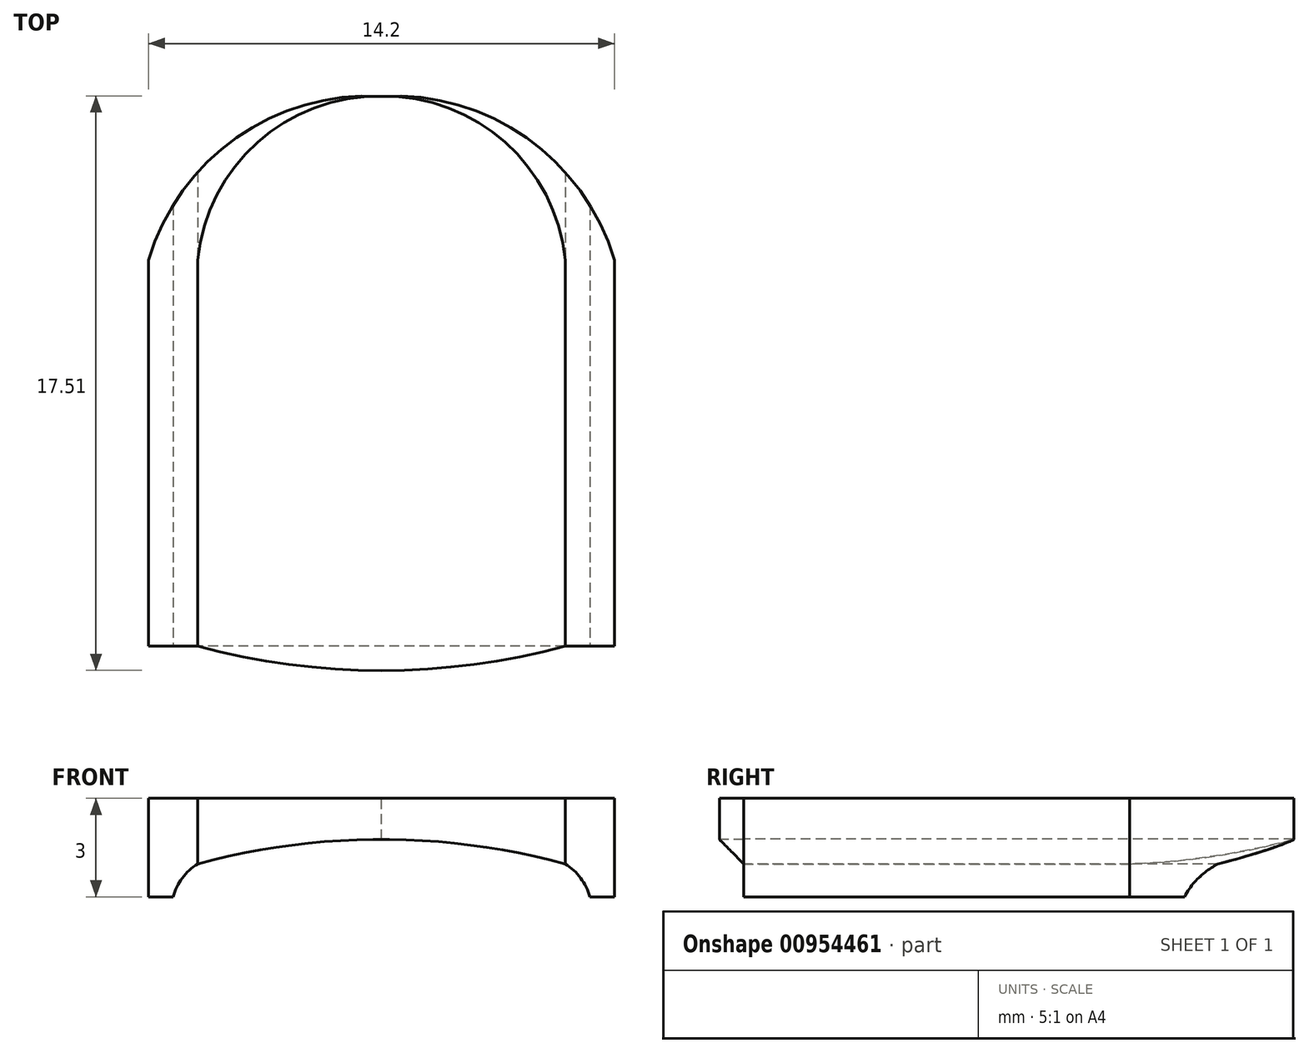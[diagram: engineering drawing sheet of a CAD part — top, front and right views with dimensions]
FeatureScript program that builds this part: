
annotation { "Feature Type Name" : "Feature", "Feature Type Description" : "" }
export const myFeature = defineFeature(function(context is Context, id is Id, definition is map)
    precondition{}
    {
        {
            var Q0;
            Q0=qCreatedBy(makeId("Top.planeOp"),FACE);
            var sketch = newSketch(context, id + "F0", { "sketchPlane" : qUnion([Q0])});
            skLineSegment(sketch, "E0", {"start": v(5.6, 1.44) * mm, "end": v(5.6, 4.94) * mm, "construction": true});
            skLineSegment(sketch, "E1", {"start": v(5.6, 4.94) * mm, "end": v(5.6, 13.94) * mm, "construction": true});
            skLineSegment(sketch, "E2", {"start": v(5.6, 13.94) * mm, "end": v(5.6, 18.94) * mm, "construction": true});
            skLineSegment(sketch, "E3", {"start": v(5.6, 4.94) * mm, "end": v(1.09, 3.3) * mm, "construction": true});
            skLineSegment(sketch, "E4", {"start": v(0, 13.94) * mm, "end": v(5.6, 13.94) * mm, "construction": true});
            skArc(sketch, "E5", {"start": v(5.6, 18.94) * mm, "mid": v(1.82, 17.53) * mm, "end": v(0, 13.94) * mm});
            skArc(sketch, "E6.MirrorCS", {"start": v(5.6, 18.94) * mm, "mid": v(9.38, 17.53) * mm, "end": v(11.2, 13.94) * mm});
            skLineSegment(sketch, "E7", {"start": v(1.09, 3.3) * mm, "end": v(0, 2.18) * mm, "construction": true});
            skLineSegment(sketch, "E8", {"start": v(0, 13.94) * mm, "end": v(0, 2.18) * mm});
            skArc(sketch, "E9", {"start": v(0, 2.18) * mm, "mid": v(2.78, 1.62) * mm, "end": v(5.6, 1.44) * mm});
            skLineSegment(sketch, "E10.MirrorCS", {"start": v(11.2, 13.94) * mm, "end": v(11.2, 2.18) * mm});
            skArc(sketch, "E11.MirrorCS", {"start": v(11.2, 2.18) * mm, "mid": v(8.42, 1.62) * mm, "end": v(5.6, 1.44) * mm});
            skLineSegment(sketch, "E12.MirrorCS", {"start": v(11.2, 13.94) * mm, "end": v(5.6, 13.94) * mm, "construction": true});
            skLineSegment(sketch, "E13.MirrorCS", {"start": v(5.6, 4.94) * mm, "end": v(10.11, 3.3) * mm, "construction": true});
            skLineSegment(sketch, "E14.MirrorCS", {"start": v(10.11, 3.3) * mm, "end": v(11.2, 2.18) * mm, "construction": true});
            skSolve(sketch);
        }
        {
            var Q0;
            Q0=makeQuery(id+"F0.imprint","IMPRINT",FACE,{"disambiguationData":[TD([[makeQuery(id+"F0.imprint","IMPRINT",EDGE,{"derivedFrom":sQuery(id+"F0.wireOp",EDGE,"E5")}),1.0]])]});
            extrude(context, id + "F1", {"entities" : qUnion([Q0]), "depth" : 2 * mm, "offsetDistance" : 25 * mm});
        }
        {
            var Q0;
            Q0=qCreatedBy(makeId("Front.planeOp"),FACE);
            var sketch = newSketch(context, id + "F2", { "sketchPlane" : qUnion([Q0])});
            skPoint(sketch, "E15", {"position": v(5.6, 1) * mm});
            skLineSegment(sketch, "E16", {"start": v(5.6, 1) * mm, "end": v(5.6, 0) * mm, "construction": true});
            skPoint(sketch, "E17", {"position": v(5.6, 0.5) * mm});
            skPoint(sketch, "E18", {"position": v(5.6, 0.75) * mm});
            skLineSegment(sketch, "E19", {"start": v(0, 0) * mm, "end": v(0, 2) * mm, "construction": true});
            skLineSegment(sketch, "E20", {"start": v(11.2, 2) * mm, "end": v(11.2, 0) * mm, "construction": true});
            skLineSegment(sketch, "E21", {"start": v(0, 2) * mm, "end": v(11.2, 2) * mm, "construction": true});
            skArc(sketch, "E22", {"start": v(11.2, 0) * mm, "mid": v(5.6, 0.75) * mm, "end": v(0, 0) * mm});
            skLineSegment(sketch, "E23", {"start": v(0, 0) * mm, "end": v(11.2, 0) * mm});
            skSolve(sketch);
        }
        {
            var Q0;
            Q0=makeQuery(id+"F2.imprint","IMPRINT",FACE,{"disambiguationData":[TD([[makeQuery(id+"F2.imprint","IMPRINT",EDGE,{"derivedFrom":sQuery(id+"F2.wireOp",EDGE,"E22")}),1.0]])]});
            extrude(context, id + "F3", {"entities" : qUnion([Q0]), "operationType" : NewBodyOperationType.REMOVE, "oppositeDirection" : true, "depth" : 25 * mm, "offsetDistance" : 25 * mm});
        }
        {
            var Q0;
            Q0=makeQuery(id+"F1.opExtrude","CAP_FACE",FACE,{"disambiguationData":[OSD([sQuery(id+"F0.wireOp",EDGE,"E5"),sQuery(id+"F0.wireOp",EDGE,"E6.MirrorCS"),sQuery(id+"F0.wireOp",EDGE,"E8"),sQuery(id+"F0.wireOp",EDGE,"E9"),sQuery(id+"F0.wireOp",EDGE,"E10.MirrorCS"),sQuery(id+"F0.wireOp",EDGE,"E11.MirrorCS")])],"isStart":false});
            var sketch = newSketch(context, id + "F4", { "sketchPlane" : qUnion([Q0])});
            skLineSegment(sketch, "E24.bottom", {"start": v(0, 2.18) * mm, "end": v(-1.5, 2.18) * mm});
            skLineSegment(sketch, "E24.top", {"start": v(0, 13.94) * mm, "end": v(-1.5, 13.94) * mm});
            skLineSegment(sketch, "E24.left", {"start": v(0, 2.18) * mm, "end": v(0, 13.94) * mm});
            skLineSegment(sketch, "E24.right", {"start": v(-1.5, 2.18) * mm, "end": v(-1.5, 13.94) * mm});
            skLineSegment(sketch, "E25.bottom", {"start": v(11.2, 2.18) * mm, "end": v(12.7, 2.18) * mm});
            skLineSegment(sketch, "E25.top", {"start": v(11.2, 13.94) * mm, "end": v(12.7, 13.94) * mm});
            skLineSegment(sketch, "E25.left", {"start": v(11.2, 2.18) * mm, "end": v(11.2, 13.94) * mm});
            skLineSegment(sketch, "E25.right", {"start": v(12.7, 2.18) * mm, "end": v(12.7, 13.94) * mm});
            skArc(sketch, "E26", {"start": v(5.6, 18.94) * mm, "mid": v(1.18, 17.67) * mm, "end": v(-1.5, 13.94) * mm});
            skArc(sketch, "E27", {"start": v(12.7, 13.94) * mm, "mid": v(10.02, 17.67) * mm, "end": v(5.6, 18.94) * mm});
            skSolve(sketch);
        }
        {
            var Q0;
            Q0=makeQuery(id+"F4.imprint","IMPRINT",FACE,{"disambiguationData":[TD([[makeQuery(id+"F4.imprint","IMPRINT",EDGE,{"derivedFrom":sQuery(id+"F4.wireOp",EDGE,"E25.top")}),1.0]])]});
            var Q1;
            Q1=makeQuery(id+"F4.imprint","IMPRINT",FACE,{"disambiguationData":[TD([[makeQuery(id+"F4.imprint","IMPRINT",EDGE,{"derivedFrom":sQuery(id+"F4.wireOp",EDGE,"E25.bottom")}),1.0]])]});
            var Q2;
            Q2=makeQuery(id+"F4.imprint","IMPRINT",FACE,{"disambiguationData":[TD([[makeQuery(id+"F4.imprint","IMPRINT",EDGE,{"derivedFrom":sQuery(id+"F4.wireOp",EDGE,"E24.top")}),-1.0]])]});
            var Q3;
            Q3=makeQuery(id+"F4.imprint","IMPRINT",FACE,{"disambiguationData":[TD([[makeQuery(id+"F4.imprint","IMPRINT",EDGE,{"derivedFrom":sQuery(id+"F4.wireOp",EDGE,"E24.bottom")}),-1.0]])]});
            extrude(context, id + "F5", {"entities" : qUnion([Q0, Q1, Q2, Q3]), "oppositeDirection" : true, "depth" : 3 * mm, "offsetDistance" : 25 * mm});
        }
        {
            var Q0;
            Q0=makeQuery(id+"F5.opExtrude","SWEPT_FACE",FACE,{"disambiguationData":[OSD([sQuery(id+"F4.wireOp",EDGE,"E24.bottom")])]});
            var sketch = newSketch(context, id + "F6", { "sketchPlane" : qUnion([Q0])});
            skArc(sketch, "E28", {"start": v(0, 0) * mm, "mid": v(-0.47, -0.43) * mm, "end": v(-0.75, -1) * mm});
            skSolve(sketch);
        }
        {
            var Q0;
            {var subQ0=sQuery(id+"F6.wireOp",EDGE,"E28");Q0=makeQuery(id+"F6.imprint","IMPRINT",FACE,{"disambiguationData":[TD([[makeQuery(id+"F6.imprint","IMPRINT",EDGE,{"derivedFrom":subQ0}),1.0]])]});}
            extrude(context, id + "F7", {"entities" : qUnion([Q0]), "operationType" : NewBodyOperationType.REMOVE, "oppositeDirection" : true, "depth" : 25 * mm, "offsetDistance" : 25 * mm});
        }
        {
            var Q0;
            Q0=makeQuery(id+"F5.opExtrude","SWEPT_FACE",FACE,{"disambiguationData":[OSD([sQuery(id+"F4.wireOp",EDGE,"E25.bottom")])]});
            var sketch = newSketch(context, id + "F8", { "sketchPlane" : qUnion([Q0])});
            skArc(sketch, "E29", {"start": v(11.95, -1) * mm, "mid": v(11.67, -0.43) * mm, "end": v(11.2, 0) * mm});
            skArc(sketch, "E30", {"start": v(11.2, 0) * mm, "mid": v(5.6, 0.76) * mm, "end": v(0, 0) * mm});
            skLineSegment(sketch, "E31", {"start": v(0, 0) * mm, "end": v(0, -1) * mm});
            skLineSegment(sketch, "E32", {"start": v(0, -1) * mm, "end": v(11.95, -1) * mm});
            skSolve(sketch);
        }
        {
            var Q0;
            Q0 = qSketchRegion(id + "F8", true);
            extrude(context, id + "F9", {"entities" : qUnion([Q0]), "operationType" : NewBodyOperationType.REMOVE, "endBound" : BoundingType.THROUGH_ALL, "oppositeDirection" : true, "depth" : 25 * mm, "offsetDistance" : 25 * mm});
        }
    });
